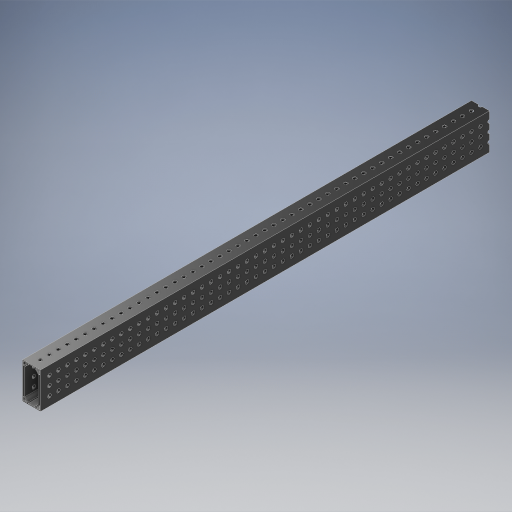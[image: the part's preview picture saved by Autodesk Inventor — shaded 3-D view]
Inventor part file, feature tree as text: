
AUTODESK INVENTOR PART (.ipt)
format: ipt  version: 2024.2 (Build 282272000, 272)  size: 1,205,248 bytes
history: native  units: in
note: dims shown in document units (in); Inventor stores cm internally (conversion verified against a paired STEP export)
features: other x13, extrude x9, hole x3, pattern_linear x3, mirror x3, sheet_metal_op x1, plane x1
ambient origin geometry x8: Origin, YZ Plane, XZ Plane, XY Plane, X Axis, Y Axis, Z Axis, Center Point
bodies: Solid1 (feature_tree)
feature tree (33):
  other  "MAXTube"
  other  "Blocks"
  other  "Base Sketch"
  extrude  "Base"  Depth=2.0in
  extrude  "MAX Corner"  Depth=1.0in
  extrude  "MAX Corner Cut"  Depth=0.125in
  extrude  "Scribe Lines"  Depth=0.04in
  other  "Side Middle"
  other  "Top Middle"
  other  "Side Holes Sketch"
  hole  "Top Side Hole"  [1 undecoded]
  hole  "Mid Side Hole"  [1 undecoded]
  hole  "Btm Side Hole"  [1 undecoded]
  pattern_linear  "Side Holes"  Spacing1=0.04in  [1 undecoded]
  mirror  "Side Mirror"
  extrude  "MAXTube Hole"  Depth=0.04in
  extrude  "MAXTube Outside"  Depth=25.0in
  pattern_linear  "MAXTube Pattern"  Spacing1=0.0in  [1 undecoded]
  mirror  "MAXTube Mirror"
  extrude  "Left Top Hole"  Depth=25.0in
  extrude  "Mid Top Hole"  TaperAngle=0.0deg  [1 undecoded]
  extrude  "Right Top Hole"  TaperAngle=0.0deg  [1 undecoded]
  pattern_linear  "Top Holes"  Spacing1=0.005in  [1 undecoded]
  mirror  "Top Mirror"
  sheet_metal_op  "Corner"
  plane  "Work Plane3"
  other  "Corner:5"
  other  "Corner:6"
  other  "Corner:7"
  other  "Corner:8"
  other  "MAXTube:1"
  other  "MAXTube:2"
  other  "MAXTube:3"
note: 8 required parameter values undecoded (feature->parameter linkage not recoverable at this tier; creation-order binding heuristic only, values carry confidence <= 0.55)
